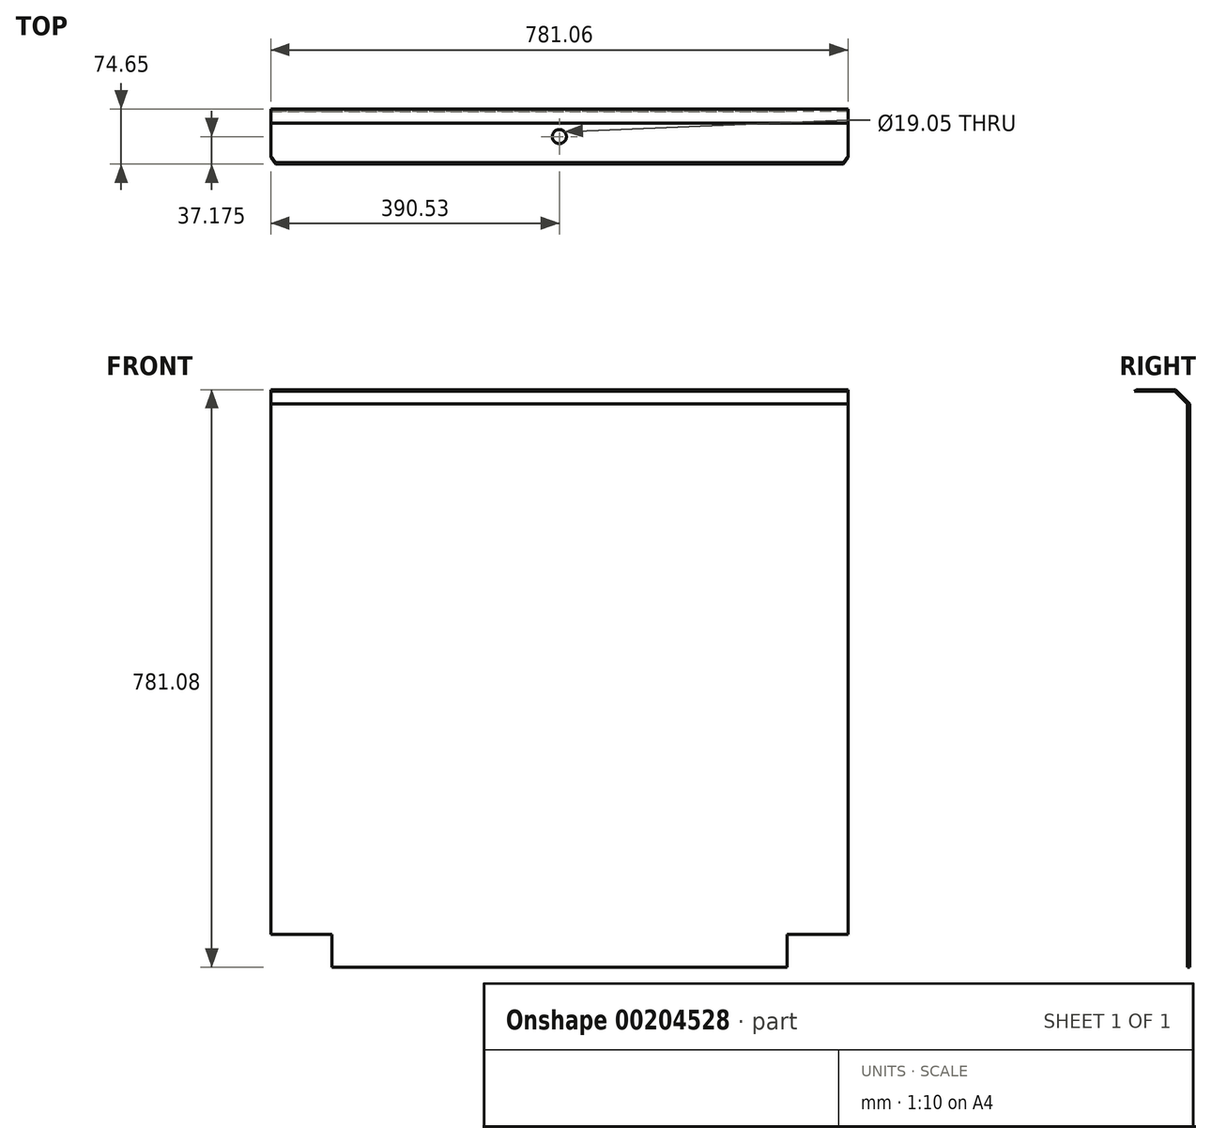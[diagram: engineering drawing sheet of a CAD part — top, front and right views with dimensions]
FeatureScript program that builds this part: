
annotation { "Feature Type Name" : "Feature", "Feature Type Description" : "" }
export const myFeature = defineFeature(function(context is Context, id is Id, definition is map)
    precondition{}
    {
        {
            var Q0;
            Q0=qCreatedBy(makeId("Front.planeOp"),FACE);
            var sketch = newSketch(context, id + "F0", { "sketchPlane" : qUnion([Q0])});
            skLineSegment(sketch, "E0", {"start": v(-307.98, -381) * mm, "end": v(307.98, -381) * mm});
            skLineSegment(sketch, "E1", {"start": v(390.53, -336.55) * mm, "end": v(390.53, 381) * mm});
            skLineSegment(sketch, "E2", {"start": v(390.53, 381) * mm, "end": v(-390.53, 381) * mm});
            skLineSegment(sketch, "E3", {"start": v(-390.53, 381) * mm, "end": v(-390.53, -336.55) * mm});
            skLineSegment(sketch, "E4", {"start": v(-390.53, -336.55) * mm, "end": v(-307.98, -336.55) * mm});
            skLineSegment(sketch, "E5", {"start": v(-307.98, -336.55) * mm, "end": v(-307.98, -381) * mm});
            skLineSegment(sketch, "E6.MirrorCS", {"start": v(390.53, -336.55) * mm, "end": v(307.98, -336.55) * mm});
            skLineSegment(sketch, "E7.MirrorCS", {"start": v(307.98, -336.55) * mm, "end": v(307.98, -381) * mm});
            skPoint(sketch, "E8.orphan", {"position": v(-390.53, -381) * mm});
            skSolve(sketch);
        }
        {
            var Q0;
            Q0=makeQuery(id+"F0.imprint","IMPRINT",FACE,{"disambiguationData":[TD([[makeQuery(id+"F0.imprint","IMPRINT",EDGE,{"derivedFrom":sQuery(id+"F0.wireOp",EDGE,"E0")}),1.0]])]});
            extrude(context, id + "F1", {"entities" : qUnion([Q0]), "depth" : 3.17 * mm});
        }
        {
            var Q0;
            Q0=makeQuery(id+"F1.opExtrude","SWEPT_FACE",FACE,{"disambiguationData":[OSD([sQuery(id+"F0.wireOp",EDGE,"E3")])]});
            var sketch = newSketch(context, id + "F2", { "sketchPlane" : qUnion([Q0])});
            skLineSegment(sketch, "E9", {"start": v(1.59, 381) * mm, "end": v(19.55, 398.96) * mm});
            skLineSegment(sketch, "E10", {"start": v(19.55, 398.96) * mm, "end": v(73.52, 398.96) * mm});
            skSolve(sketch);
        }
        {
            var Q0;
            Q0=makeQuery(id+"F1.opExtrude","SWEPT_FACE",FACE,{"disambiguationData":[OSD([sQuery(id+"F0.wireOp",EDGE,"E2")])]});
            var Q1;
            Q1=sQuery(id+"F2.wireOp",EDGE,"E9");
            var Q2;
            Q2=sQuery(id+"F2.wireOp",EDGE,"E10");
            sweep(context, id + "F3", {"operationType" : NewBodyOperationType.ADD, "profiles" : qUnion([Q0]), "path" : qUnion([Q1, Q2])});
        }
        {
            var Q0;
            Q0=makeQuery(id+"F3.opSweep","CAP_EDGE",EDGE,{"disambiguationData":[OSD([sQuery(id+"F0.wireOp",EDGE,"E2"),sQuery(id+"F0.wireOp",EDGE,"E3"),sQuery(id+"F2.wireOp",VERTEX,"E10.end")])],"isStart":false});
            var Q1;
            Q1=makeQuery(id+"F3.opSweep","CAP_EDGE",EDGE,{"disambiguationData":[OSD([sQuery(id+"F0.wireOp",EDGE,"E1"),sQuery(id+"F0.wireOp",EDGE,"E2"),sQuery(id+"F2.wireOp",VERTEX,"E10.end")])],"isStart":false});
            chamfer(context, id + "F4", {"entities" : qUnion([Q0, Q1]), "width" : 6.35 * mm, "tangentPropagation" : true});
        }
        {
            var Q0;
            {var subQ0=sQuery(id+"F2.wireOp",EDGE,"E10");var subQ1=sQuery(id+"F0.wireOp",EDGE,"E2");Q0=makeQuery(id+"F3.opSweep","SWEPT_FACE",FACE,{"disambiguationData":[OSD([subQ1,subQ0]),TDD([makeQuery(id+"F1.opExtrude","CAP_EDGE",EDGE,{"disambiguationData":[OSD([subQ1])],"isStart":true}),subQ0])]});}
            var sketch = newSketch(context, id + "F5", { "sketchPlane" : qUnion([Q0])});
            skLineSegment(sketch, "E11", {"start": v(0, -72.4) * mm, "end": v(0, -37.48) * mm});
            skSolve(sketch);
        }
        {
            var Q0;
            Q0=sQuery(id+"F5.wireOp",VERTEX,"E11.end");
            var Q1;
            Q1=makeQuery(id+"F1.opExtrude","SWEPT_BODY",BODY,{"disambiguationData":[OSD([sQuery(id+"F0.wireOp",EDGE,"E0"),sQuery(id+"F0.wireOp",EDGE,"E1"),sQuery(id+"F0.wireOp",EDGE,"E2"),sQuery(id+"F0.wireOp",EDGE,"E3"),sQuery(id+"F0.wireOp",EDGE,"E4"),sQuery(id+"F0.wireOp",EDGE,"E5"),sQuery(id+"F0.wireOp",EDGE,"E6.MirrorCS"),sQuery(id+"F0.wireOp",EDGE,"E7.MirrorCS")])]});
            hole(context, id + "F6", {"style" : HoleStyle.SIMPLE, "endStyle" : HoleEndStyle.BLIND, "holeDiameter" : 19.05 * mm, "holeDepth" : 1524 * mm, "locations" : qUnion([Q0]), "scope" : qUnion([Q1])});
        }
    });
